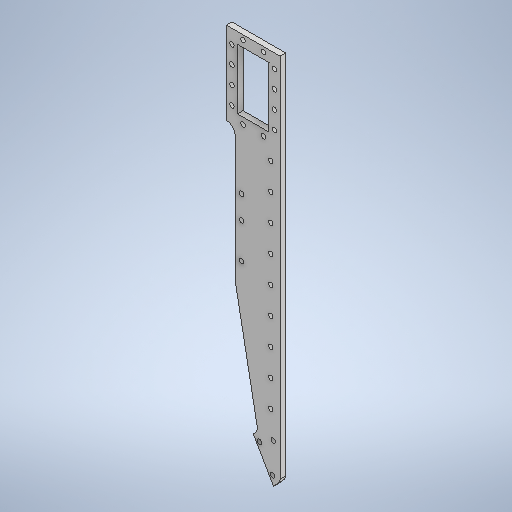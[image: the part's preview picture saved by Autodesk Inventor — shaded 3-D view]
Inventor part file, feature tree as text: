
AUTODESK INVENTOR PART (.ipt)
format: ipt  version: 2025.1 (Build 291241000, 241)  size: 373,760 bytes
history: native  units: mm
features: sketch x7, hole x5, extrude x2, plane x2, mirror x2
ambient origin geometry x8: Origin, YZ Plane, XZ Plane, XY Plane, X Axis, Y Axis, Z Axis, Center Point
bodies: Volumenkörper1 (feature_tree)
feature tree (18):
  extrude  "Extrusion1"  Depth=9.5mm
  extrude  "Extrusion2"  Depth=120.0mm
  hole  "Bohrung1"  [1 undecoded]
  hole  "Bohrung2"  [1 undecoded]
  plane  "Arbeitsebene1"
  mirror  "Spiegeln1"
  plane  "Arbeitsebene2"
  mirror  "Spiegeln2"
  hole  "Bohrung3"  [1 undecoded]
  hole  "Bohrung4"  [1 undecoded]
  hole  "Bohrung5"  [1 undecoded]
  sketch  "Skizze1"  dims[d1=58.0mm d2=9.5mm]
  sketch  "Skizze2"  dims[d3=89.0mm d4=120.0mm]
  sketch  "Skizze3"  dims[d7=406.0mm d8=44.0mm]
  sketch  "Skizze4"  dims[d9=30.0deg d10=6.0mm]
  sketch  "Skizze5"  dims[d11=126.0mm d12=29.0mm]
  sketch  "Skizze6"  dims[d13=6.0mm d14=6.0mm d15=0.0mm]
  sketch  "Skizze8"  dims[d16=34.0mm d17=65.0mm d18=12.0mm d19=6.0mm d20=0.0mm d21=11.0mm d22=11.0mm d23=5.0mm d24=5.0mm d25=6.0mm d26=4.0mm d27=2.0mm d28=90.0deg d29=8.0mm d30=20.594885mm d31=10.0mm d32=19.0mm d33=19.0mm d34=19.0mm d35=6.0mm d36=5.0mm d37=6.0mm d38=4.0mm d39=2.0mm d40=90.0deg d41=8.0mm d42=20.594885mm d43=-29.0mm d44=-44.5mm d45=19.0mm d46=29.0mm d47=29.0mm d48=29.0mm d49=29.0mm d50=29.0mm d51=29.0mm d52=29.0mm d53=29.0mm d54=10.0mm d55=5.0mm d56=6.0mm d57=4.0mm d58=2.0mm d59=90.0deg d60=8.0mm d61=0.0mm d62=51.0mm d63=25.0mm d64=38.0mm d65=7.0mm d66=5.0mm d67=6.0mm d68=4.0mm d69=2.0mm d70=90.0deg d71=8.0mm d72=0.0mm d80=4.917mm d81=12.0mm d82=4.0mm d83=2.0mm d84=90.0deg d85=8.0mm d86=0.0mm d90=90.0deg d91=14.0mm d92=28.0mm d93=90.0deg d94=17.0mm]
note: 5 required parameter values undecoded (feature->parameter linkage not recoverable at this tier; creation-order binding heuristic only, values carry confidence <= 0.55)
